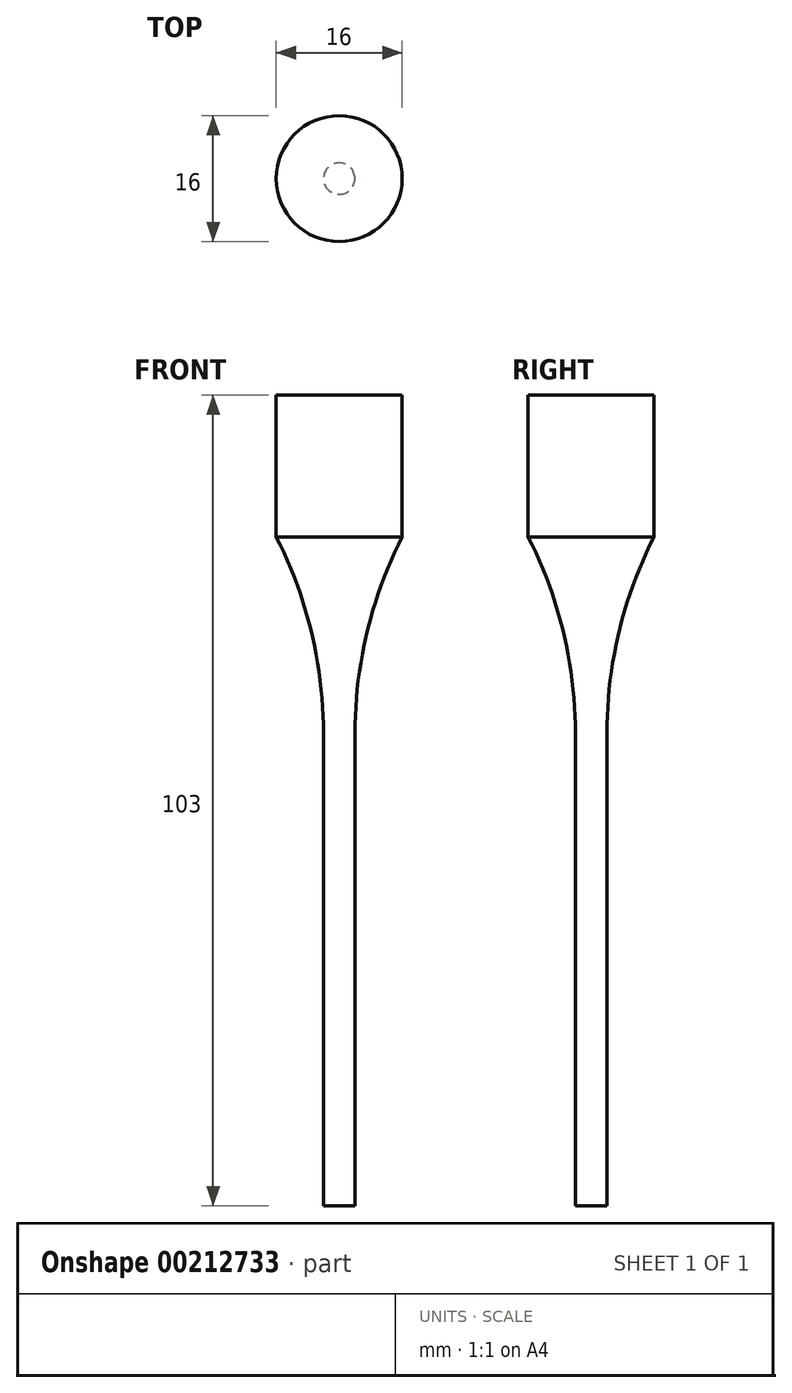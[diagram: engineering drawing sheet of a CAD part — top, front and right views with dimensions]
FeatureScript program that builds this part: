
annotation { "Feature Type Name" : "Feature", "Feature Type Description" : "" }
export const myFeature = defineFeature(function(context is Context, id is Id, definition is map)
    precondition{}
    {
        {
            var Q0;
            Q0=qCreatedBy(makeId("Front.planeOp"),FACE);
            var sketch = newSketch(context, id + "F0", { "sketchPlane" : qUnion([Q0])});
            skLineSegment(sketch, "E0", {"start": v(2, 0) * mm, "end": v(2, 60) * mm});
            skArc(sketch, "E1", {"start": v(8, 85) * mm, "mid": v(3.52, 72.85) * mm, "end": v(2, 60) * mm});
            skLineSegment(sketch, "E2", {"start": v(0, 0) * mm, "end": v(2, 0) * mm});
            skLineSegment(sketch, "E3", {"start": v(8, 85) * mm, "end": v(8, 103) * mm});
            skLineSegment(sketch, "E4", {"start": v(8, 103) * mm, "end": v(0, 103) * mm});
            skLineSegment(sketch, "E5", {"start": v(0, 103) * mm, "end": v(0, 0) * mm});
            skSolve(sketch);
        }
        {
            var Q0;
            Q0=qCreatedBy(makeId("Front.planeOp"),FACE);
            var sketch = newSketch(context, id + "F1", { "sketchPlane" : qUnion([Q0])});
            skLineSegment(sketch, "E6", {"start": v(0, 69.05) * mm, "end": v(0, 0) * mm});
            skSolve(sketch);
        }
        {
            var Q0;
            Q0=makeQuery(id+"F0.imprint","IMPRINT",FACE,{"disambiguationData":[TD([[makeQuery(id+"F0.imprint","IMPRINT",EDGE,{"derivedFrom":sQuery(id+"F0.wireOp",EDGE,"E0")}),1.0]])]});
            var Q1;
            Q1=sQuery(id+"F1.wireOp",EDGE,"E6");
            revolve(context, id + "F2", {"entities" : qUnion([Q0]), "axis" : qUnion([Q1]), "revolveType" : RevolveType.FULL});
        }
    });
